# Revit family: URBANE II WALL BASIN NTH NOF
name_source: partatom
category: Specialty Equipment
units: mm (PartAtom-declared; Revit-internal decimal feet)

## family parameters
Cut with Voids When Loaded = Yes
Host = Face
OmniClass Number = 23.45.05.14.14
OmniClass Title = Sinks/Lavatories
Part Type = Normal
Room Calculation Point = No
Round Connector Dimension = Use Radius
Shared = No

## types (2) — shared parameters
Assembly Code = D2010400
Default Elevation = 900 mm
Manufacturer = GWA Bathrooms & Kitchens
Material_Base = GWA-Porcelain-White
URL = https://www.caroma.com.au

## per-type parameters (varying)
| type | Model | TapHole | TapHoleCutout |
| URBANE II WALL BASIN NTH NOF | 878600W | No | 20 mm  [stored 0.0656168 ft] |
| URBANE II WALL BASIN 1TH NOF | 878610W | Yes | -50 mm |

note: column(s) folded — value = type name in every type: Description

note: [stored X ft] marks values corroborated as IEEE doubles in the binary element streams (Revit-internal decimal feet)

## geometry (parser evidence)
native form markers: Sweep x2
no freeform markers — native parametric forms only
